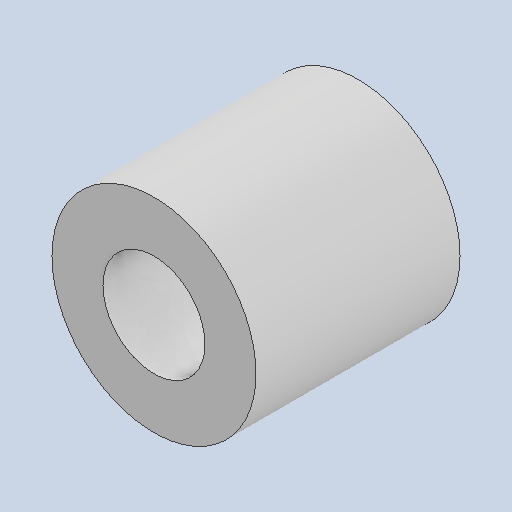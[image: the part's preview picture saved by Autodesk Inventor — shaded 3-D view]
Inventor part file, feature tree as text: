
AUTODESK INVENTOR PART (.ipt)
format: ipt  version: 2024.3 (Build 283343000, 343)  size: 102,400 bytes
history: native  units: mm
features: other x1, extrude x1, sketch x1
ambient origin geometry x8: Origin, YZ Plane, XZ Plane, XY Plane, X Axis, Y Axis, Z Axis, Center Point
bodies: Body1 (feature_tree)
feature tree (3):
  other  "ソリッド1"
  extrude  "押し出し1"  Depth=10.0mm
  sketch  "スケッチ1"
